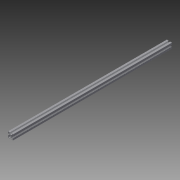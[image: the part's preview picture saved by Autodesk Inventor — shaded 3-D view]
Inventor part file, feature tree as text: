
AUTODESK INVENTOR PART (.ipt)
format: ipt  version: 2015 (Build 190159000, 159)  size: 165,888 bytes
history: native  units: in
note: dims shown in document units (in); Inventor stores cm internally (conversion verified against a paired STEP export)
features: extrude x1, fillet x1, sketch x1
ambient origin geometry x8: Origin, YZ Plane, XZ Plane, XY Plane, X Axis, Y Axis, Z Axis, Center Point
bodies: Solid1 (feature_tree)
feature tree (3):
  extrude  "Extrusion1"  Depth=23.622in TaperAngle=0.0deg
  fillet  "Fillet1"  Radius=0.0197in
  sketch  "Sketch1"  dims[d0=0.7874in d1=0.7874in d2=0.1969in d3=0.0472in d4=0.0472in d5=0.0472in d6=0.0472in d7=0.7874in d8=0.0472in d9=0.0472in d10=0.0472in d11=0.0472in d12=0.0472in d13=0.7874in d14=23.622in d15=0.0in d16=0.0197in]
